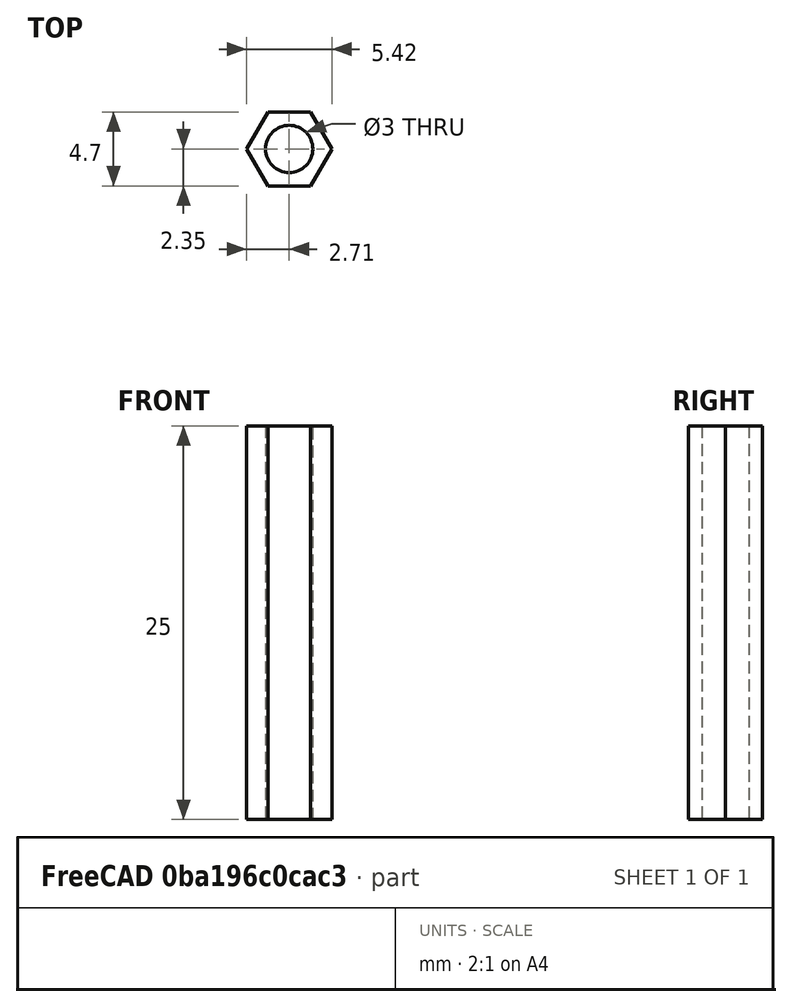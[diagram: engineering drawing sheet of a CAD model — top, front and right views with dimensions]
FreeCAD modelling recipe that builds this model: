
FCSTD DOCUMENT  (FreeCAD 0.18.4R)
Label: coxial_M3_25mm
License: All rights reserved
LicenseURL: http://en.wikipedia.org/wiki/All_rights_reserved
objects: Sketcher::SketchObject×1, PartDesign::Pad×1, PartDesign::Body×1
note: 4 computed .brp shape members not serialized (recipe doc carries the construction recipe); baked Part::Feature solids carry a one-line shape summary decoded from their .brp

FEATURE [Sketcher::SketchObject] Sketch
  MapMode = 5
  Support = -> [XY_Plane]
  sketch-geometry (8):
    g0: Circle CenterX=0 CenterY=0 CenterZ=0 NormalX=0 NormalY=0 NormalZ=1 AngleXU=0 Radius=1.5
    g1: LineSegment StartX=1.35677 StartY=-2.35 StartZ=0 EndX=2.71355 EndY=0 EndZ=0
    g2: LineSegment StartX=2.71355 StartY=0 StartZ=0 EndX=1.35677 EndY=2.35 EndZ=0
    g3: LineSegment StartX=1.35677 StartY=2.35 StartZ=0 EndX=-1.35677 EndY=2.35 EndZ=0
    g4: LineSegment StartX=-1.35677 StartY=2.35 StartZ=0 EndX=-2.71355 EndY=0 EndZ=0
    g5: LineSegment StartX=-2.71355 StartY=0 StartZ=0 EndX=-1.35677 EndY=-2.35 EndZ=0
    g6: LineSegment StartX=-1.35677 StartY=-2.35 StartZ=0 EndX=1.35677 EndY=-2.35 EndZ=0
    g7: Circle [constr] CenterX=0 CenterY=0 CenterZ=0 NormalX=0 NormalY=0 NormalZ=1 AngleXU=0 Radius=2.71355
  constraints (18):
    c: Radius(g0) = 1.5
    c: Coincident(g0,g-1)
    c: Coincident(g1,g2)
    c: Coincident(g2,g3)
    c: Coincident(g3,g4)
    c: Coincident(g4,g5)
    c: Coincident(g5,g6)
    c: Coincident(g6,g1)
    c: Equal(g1, g2-g6) x5
    c: PointOnObject(g1,g7)
    c: PointOnObject(g2,g7)
    c: PointOnObject(g3,g7)
    c: PointOnObject(g4,g7)
    c: PointOnObject(g5,g7)
    c: PointOnObject(g6,g7)
    c: Coincident(g7,g0)
    c: Distance(g2,g4) = 4.7
    c: Horizontal(g3)
FEATURE [PartDesign::Pad] Pad
  Length = 25
  Length2 = 100
  Profile = -> Sketch
  Type = 0
FEATURE [PartDesign::Body] Body
  Group = -> [Sketch,Pad]
  Origin = -> Origin
  Tip = -> Pad
